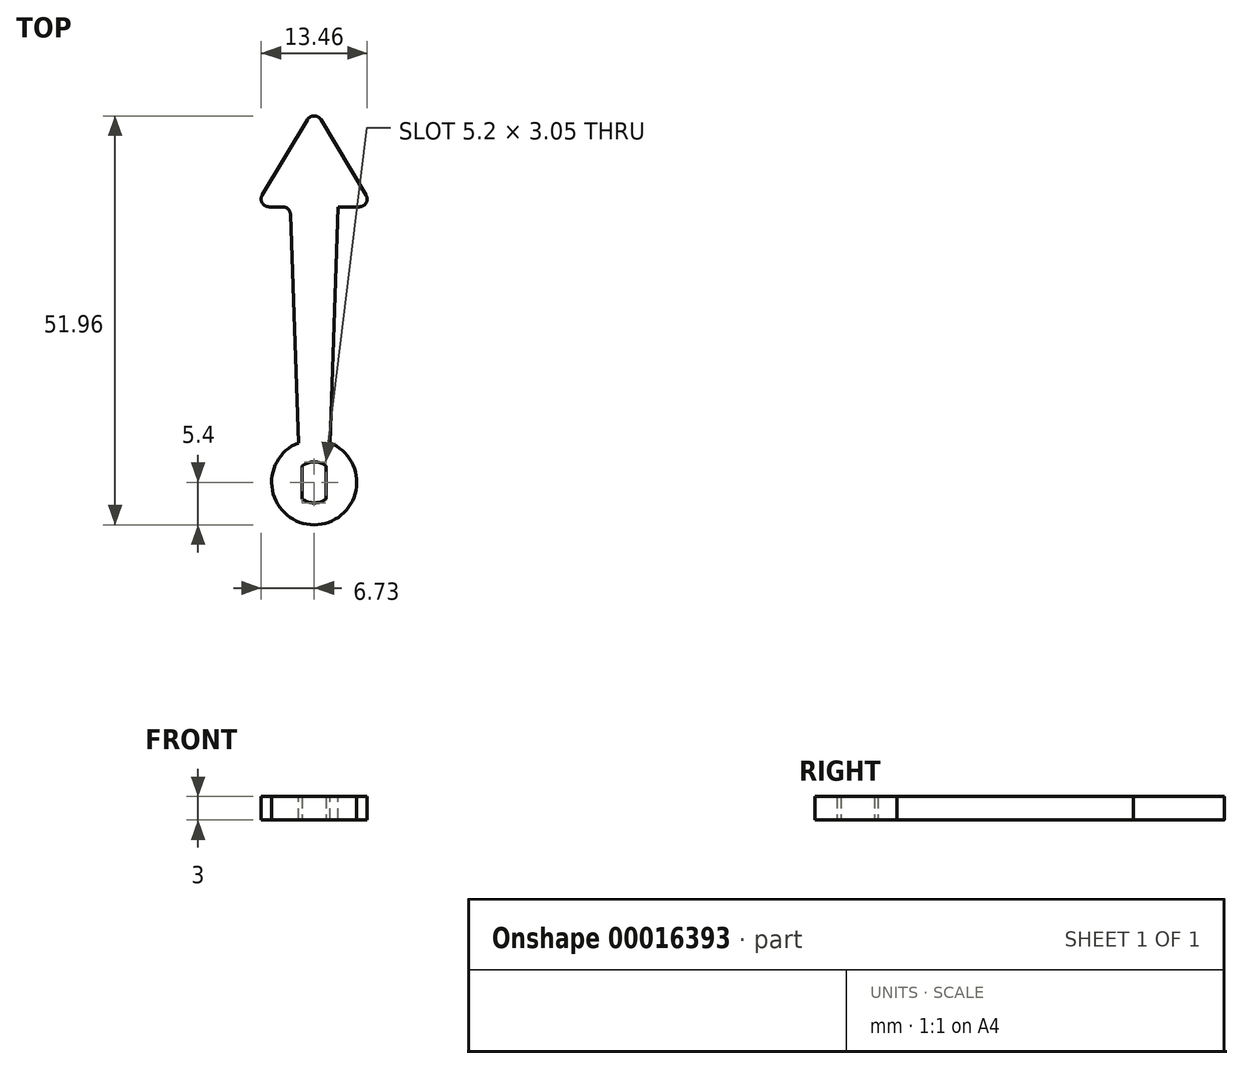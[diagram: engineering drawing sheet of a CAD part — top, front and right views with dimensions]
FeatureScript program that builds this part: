
annotation { "Feature Type Name" : "Feature", "Feature Type Description" : "" }
export const myFeature = defineFeature(function(context is Context, id is Id, definition is map)
    precondition{}
    {
        {
            var Q0;
            Q0=qCreatedBy(makeId("Top.planeOp"),FACE);
            var sketch = newSketch(context, id + "F0", { "sketchPlane" : qUnion([Q0])});
            skArc(sketch, "E0", {"start": v(1.52, 2.1) * mm, "mid": v(0, 2.6) * mm, "end": v(-1.53, 2.1) * mm});
            skCircle(sketch, "E1", {"center": v(0, 0) * mm, "radius": 5.4 * mm});
            skLineSegment(sketch, "E2", {"start": v(-1.52, 2.1) * mm, "end": v(-1.52, -2.1) * mm});
            skLineSegment(sketch, "E3", {"start": v(1.53, 2.1) * mm, "end": v(1.53, -2.1) * mm});
            skArc(sketch, "E4.trimOffspring", {"start": v(-1.53, -2.1) * mm, "mid": v(0, -2.6) * mm, "end": v(1.52, -2.1) * mm});
            skSolve(sketch);
        }
        {
            var Q0;
            Q0=makeQuery(id+"F0.imprint","IMPRINT",FACE,{"disambiguationData":[TD([[makeQuery(id+"F0.imprint","IMPRINT",EDGE,{"derivedFrom":sQuery(id+"F0.wireOp",EDGE,"E0")}),-1.0]])]});
            extrude(context, id + "F1", {"entities" : qUnion([Q0]), "endBound" : BoundingType.SYMMETRIC, "depth" : 3 * mm});
        }
        {
            var Q0;
            Q0=makeQuery(id+"F1.opExtrude","CAP_FACE",FACE,{"disambiguationData":[OSD([sQuery(id+"F0.wireOp",EDGE,"E0"),sQuery(id+"F0.wireOp",EDGE,"E1"),sQuery(id+"F0.wireOp",EDGE,"E2"),sQuery(id+"F0.wireOp",EDGE,"E3"),sQuery(id+"F0.wireOp",EDGE,"E4.trimOffspring")])],"isStart":false});
            var sketch = newSketch(context, id + "F2", { "sketchPlane" : qUnion([Q0])});
            skLineSegment(sketch, "E5", {"start": v(0, 0) * mm, "end": v(0, 35) * mm, "construction": true});
            skLineSegment(sketch, "E6", {"start": v(-3.05, 35) * mm, "end": v(3.05, 35) * mm});
            skLineSegment(sketch, "E7", {"start": v(-2, 5.02) * mm, "end": v(2, 5.02) * mm});
            skLineSegment(sketch, "E8", {"start": v(-2, 5.02) * mm, "end": v(-3.05, 35) * mm});
            skLineSegment(sketch, "E9", {"start": v(2, 5.02) * mm, "end": v(3.05, 35) * mm});
            skSolve(sketch);
        }
        {
            var Q0;
            Q0=makeQuery(id+"F2.imprint","IMPRINT",FACE,{"disambiguationData":[TD([[makeQuery(id+"F2.imprint","IMPRINT",EDGE,{"derivedFrom":sQuery(id+"F2.wireOp",EDGE,"E6")}),-1.0]])]});
            var Q1;
            Q1=makeQuery(id+"F1.opExtrude","CAP_FACE",FACE,{"disambiguationData":[OSD([sQuery(id+"F0.wireOp",EDGE,"E0"),sQuery(id+"F0.wireOp",EDGE,"E1"),sQuery(id+"F0.wireOp",EDGE,"E2"),sQuery(id+"F0.wireOp",EDGE,"E3"),sQuery(id+"F0.wireOp",EDGE,"E4.trimOffspring")])],"isStart":true});
            extrude(context, id + "F3", {"entities" : qUnion([Q0]), "operationType" : NewBodyOperationType.ADD, "endBound" : BoundingType.UP_TO_SURFACE, "oppositeDirection" : true, "endBoundEntityFace" : qUnion([Q1]), "depth" : 25 * mm});
        }
        {
            var Q0;
            {var subQ0=sQuery(id+"F0.wireOp",EDGE,"E1");Q0=makeQuery(id+"F3.boolean.opBoolean","MERGE",FACE,{"derivedFrom":[makeQuery(id+"F1.opExtrude","CAP_FACE",FACE,{"disambiguationData":[OSD([sQuery(id+"F0.wireOp",EDGE,"E0"),subQ0,sQuery(id+"F0.wireOp",EDGE,"E2"),sQuery(id+"F0.wireOp",EDGE,"E3"),sQuery(id+"F0.wireOp",EDGE,"E4.trimOffspring")])],"isStart":false}),makeQuery(id+"F3.opExtrude","CAP_FACE",FACE,{"disambiguationData":[OSD([subQ0,sQuery(id+"F2.wireOp",EDGE,"E6"),sQuery(id+"F2.wireOp",EDGE,"E8"),sQuery(id+"F2.wireOp",EDGE,"E9")])],"isStart":true})]});}
            var sketch = newSketch(context, id + "F4", { "sketchPlane" : qUnion([Q0])});
            skLineSegment(sketch, "E10", {"start": v(7.5, 35) * mm, "end": v(-7.5, 35) * mm});
            skLineSegment(sketch, "E11", {"start": v(-7.5, 35) * mm, "end": v(0, 47.5) * mm});
            skLineSegment(sketch, "E12", {"start": v(0, 47.5) * mm, "end": v(7.5, 35) * mm});
            skLineSegment(sketch, "E13", {"start": v(0, 35) * mm, "end": v(0, 47.5) * mm});
            skSolve(sketch);
        }
        {
            var Q0;
            {var subQ1=sQuery(id+"F4.wireOp",EDGE,"E11");Q0=makeQuery(id+"F4.imprint","IMPRINT",FACE,{"disambiguationData":[TD([[makeQuery(id+"F4.imprint","IMPRINT",EDGE,{"derivedFrom":subQ1}),-1.0]])]});}
            var Q1;
            {var subQ1=sQuery(id+"F4.wireOp",EDGE,"E12");Q1=makeQuery(id+"F4.imprint","IMPRINT",FACE,{"disambiguationData":[TD([[makeQuery(id+"F4.imprint","IMPRINT",EDGE,{"derivedFrom":subQ1}),-1.0]])]});}
            var Q2;
            {var subQ0=sQuery(id+"F0.wireOp",EDGE,"E1");Q2=makeQuery(id+"F3.boolean.opBoolean","MERGE",FACE,{"derivedFrom":[makeQuery(id+"F1.opExtrude","CAP_FACE",FACE,{"disambiguationData":[OSD([sQuery(id+"F0.wireOp",EDGE,"E0"),subQ0,sQuery(id+"F0.wireOp",EDGE,"E2"),sQuery(id+"F0.wireOp",EDGE,"E3"),sQuery(id+"F0.wireOp",EDGE,"E4.trimOffspring")])],"isStart":true}),makeQuery(id+"F3.opExtrude","CAP_FACE",FACE,{"disambiguationData":[OSD([subQ0,sQuery(id+"F2.wireOp",EDGE,"E6"),sQuery(id+"F2.wireOp",EDGE,"E8"),sQuery(id+"F2.wireOp",EDGE,"E9")])],"isStart":false})]});}
            extrude(context, id + "F5", {"entities" : qUnion([Q0, Q1]), "operationType" : NewBodyOperationType.ADD, "endBound" : BoundingType.UP_TO_SURFACE, "oppositeDirection" : true, "endBoundEntityFace" : qUnion([Q2]), "depth" : 25 * mm});
        }
        {
            var Q0;
            Q0=makeQuery(id+"F5.opExtrude","SWEPT_EDGE",EDGE,{"disambiguationData":[OSD([sQuery(id+"F4.wireOp",EDGE,"E11"),sQuery(id+"F4.wireOp",EDGE,"E12"),sQuery(id+"F4.wireOp",EDGE,"E13")])]});
            var Q1;
            Q1=makeQuery(id+"F5.opExtrude","SWEPT_EDGE",EDGE,{"disambiguationData":[OSD([sQuery(id+"F4.wireOp",EDGE,"E10"),sQuery(id+"F4.wireOp",EDGE,"E12")])]});
            var Q2;
            Q2=makeQuery(id+"F5.opExtrude","SWEPT_EDGE",EDGE,{"disambiguationData":[OSD([sQuery(id+"F4.wireOp",EDGE,"E10"),sQuery(id+"F4.wireOp",EDGE,"E11")])]});
            var Q3;
            Q3=makeQuery(id+"F3.opExtrude","SWEPT_EDGE",EDGE,{"disambiguationData":[OSD([sQuery(id+"F2.wireOp",EDGE,"E6"),sQuery(id+"F2.wireOp",EDGE,"E8")])]});
            var Q4;
            Q4=makeQuery(id+"F3.opExtrude","SWEPT_EDGE",EDGE,{"disambiguationData":[OSD([sQuery(id+"F2.wireOp",EDGE,"E6"),sQuery(id+"F2.wireOp",EDGE,"E9")])]});
            fillet(context, id + "F6", {"entities" : qUnion([Q0, Q1, Q2, Q3, Q4]), "radius" : 1 * mm, "tangentPropagation" : true, "allowEdgeOverflow" : false});
        }
    });
